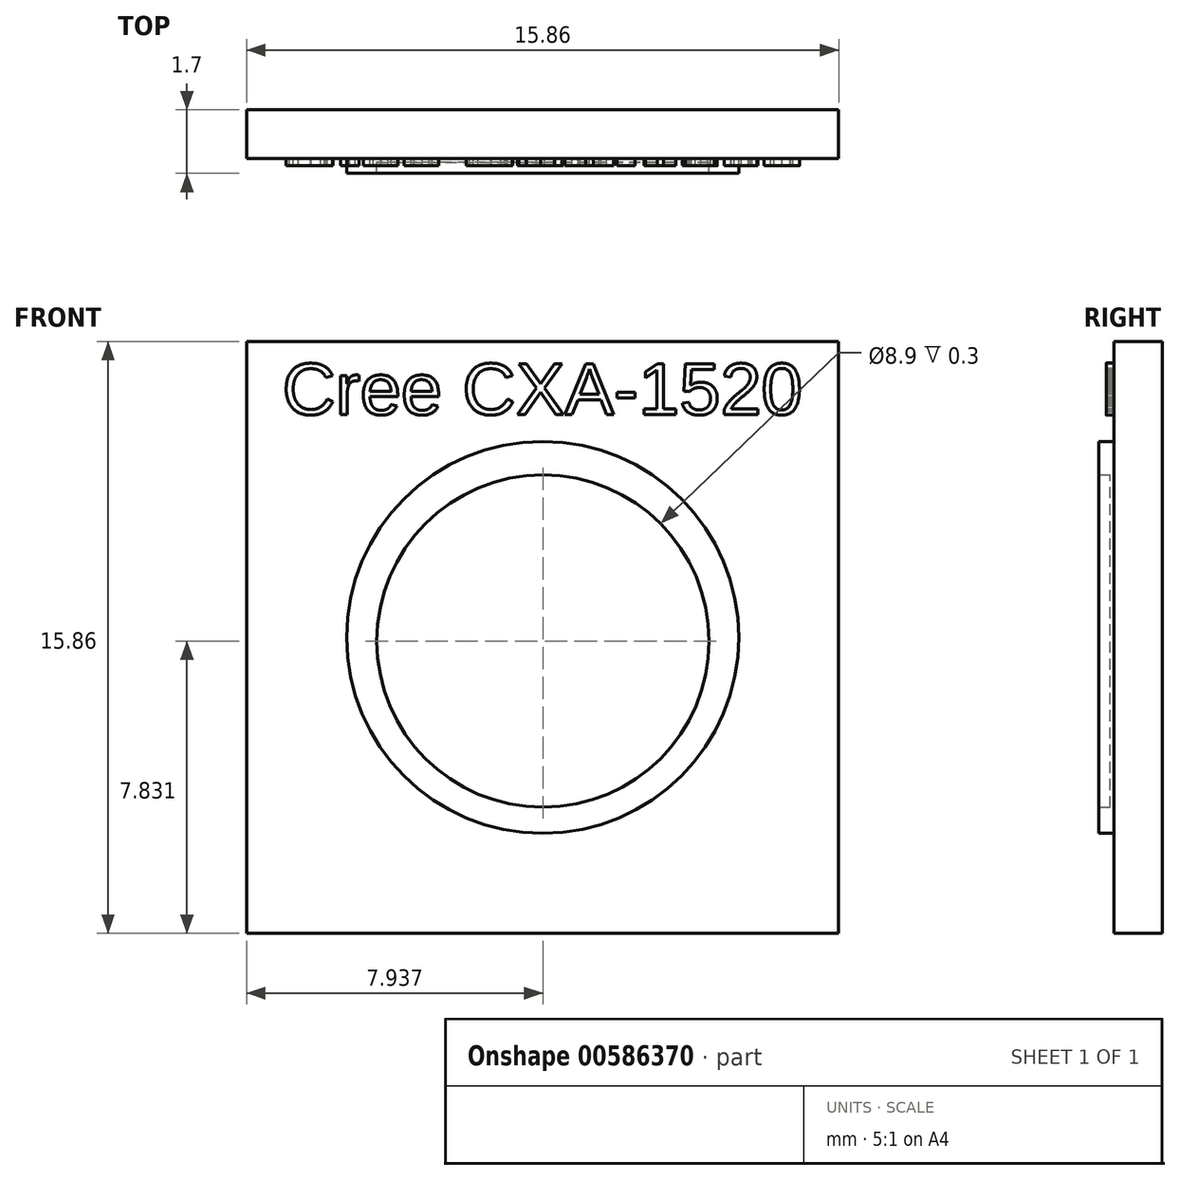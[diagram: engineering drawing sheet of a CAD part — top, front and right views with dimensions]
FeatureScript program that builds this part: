
annotation { "Feature Type Name" : "Feature", "Feature Type Description" : "" }
export const myFeature = defineFeature(function(context is Context, id is Id, definition is map)
    precondition{}
    {
        {
            var Q0;
            Q0=qCreatedBy(makeId("Front.planeOp"),FACE);
            var sketch = newSketch(context, id + "F0", { "sketchPlane" : qUnion([Q0])});
            skLineSegment(sketch, "E0.bottom", {"start": v(-7.92, -7.93) * mm, "end": v(7.93, -7.93) * mm});
            skLineSegment(sketch, "E0.top", {"start": v(-7.93, 7.93) * mm, "end": v(7.92, 7.93) * mm});
            skLineSegment(sketch, "E0.left", {"start": v(-7.92, -7.93) * mm, "end": v(-7.93, 7.93) * mm});
            skLineSegment(sketch, "E0.right", {"start": v(7.93, -7.92) * mm, "end": v(7.92, 7.93) * mm});
            skPoint(sketch, "E0.middle", {"position": v(0, 0) * mm});
            skSolve(sketch);
        }
        {
            var Q0;
            Q0=makeQuery(id+"F0.imprint","IMPRINT",FACE,{"disambiguationData":[TD([[makeQuery(id+"F0.imprint","IMPRINT",EDGE,{"derivedFrom":sQuery(id+"F0.wireOp",EDGE,"E0.bottom")}),1.0]])]});
            var sketch = newSketch(context, id + "F1", { "sketchPlane" : qUnion([Q0])});
            skCircle(sketch, "E1", {"center": v(0, 0) * mm, "radius": 5.25 * mm});
            skCircle(sketch, "E2", {"center": v(0, -0.1) * mm, "radius": 4.45 * mm});
            skSolve(sketch);
        }
        {
            var Q0;
            Q0=makeQuery(id+"F1.imprint","IMPRINT",FACE,{"disambiguationData":[TD([[makeQuery(id+"F1.imprint","IMPRINT",EDGE,{"derivedFrom":sQuery(id+"F1.wireOp",EDGE,"E2")}),1.0]])]});
            extrude(context, id + "F2", {"entities" : qUnion([Q0]), "depth" : 1.4 * mm, "offsetDistance" : 25 * mm});
        }
        {
            var Q0;
            Q0 = qSketchRegion(id + "F1", true);
            extrude(context, id + "F3", {"entities" : qUnion([Q0]), "operationType" : NewBodyOperationType.ADD, "depth" : 1.7 * mm, "offsetDistance" : 25 * mm});
        }
        {
            var Q0;
            Q0=makeQuery(id+"F0.imprint","IMPRINT",FACE,{"disambiguationData":[TD([[makeQuery(id+"F0.imprint","IMPRINT",EDGE,{"derivedFrom":sQuery(id+"F0.wireOp",EDGE,"E0.bottom")}),1.0]])]});
            extrude(context, id + "F4", {"entities" : qUnion([Q0]), "operationType" : NewBodyOperationType.ADD, "depth" : 1.3 * mm, "offsetDistance" : 25 * mm});
        }
        {
            var Q0;
            Q0=makeQuery(id+"F4.opExtrude","CAP_FACE",FACE,{"disambiguationData":[OSD([sQuery(id+"F0.wireOp",EDGE,"E0.bottom"),sQuery(id+"F0.wireOp",EDGE,"E0.top"),sQuery(id+"F0.wireOp",EDGE,"E0.left"),sQuery(id+"F0.wireOp",EDGE,"E0.right")])],"isStart":false});
            var sketch = newSketch(context, id + "F5", { "sketchPlane" : qUnion([Q0])});
            skText(sketch, "E3", { "text": "Cree CXA-1520", "fontName": "Arimo-Regular.ttf"});
            const initialGuessF5  = {"E3": [-0.00697, 0.00597, 1, 0, 0.00142]};
            skSetInitialGuess(sketch, initialGuessF5);
            skSolve(sketch);
        }
        {
            var Q0;
            Q0 = qSketchRegion(id + "F5", true);
            extrude(context, id + "F6", {"entities" : qUnion([Q0]), "operationType" : NewBodyOperationType.ADD, "depth" : .2 * mm, "offsetDistance" : 25 * mm});
        }
    });
